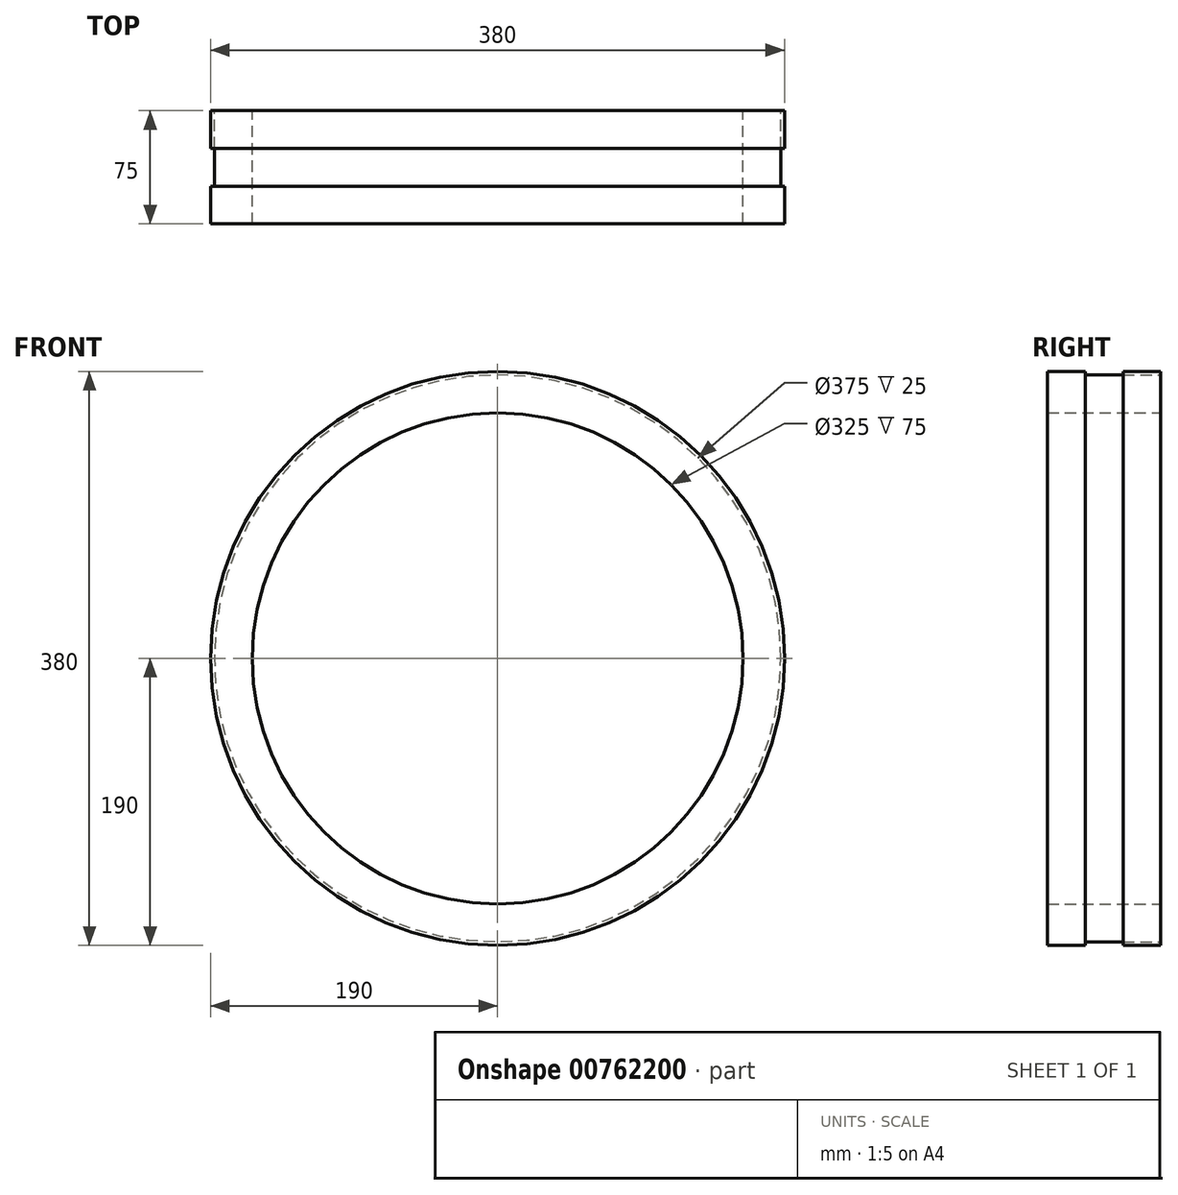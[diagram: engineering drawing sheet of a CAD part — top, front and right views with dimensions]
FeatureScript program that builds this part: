
annotation { "Feature Type Name" : "Feature", "Feature Type Description" : "" }
export const myFeature = defineFeature(function(context is Context, id is Id, definition is map)
    precondition{}
    {
        {
            var Q0;
            Q0=qCreatedBy(makeId("Front.planeOp"),FACE);
            var sketch = newSketch(context, id + "F0", { "sketchPlane" : qUnion([Q0])});
            skCircle(sketch, "E0", {"center": v(0, 0) * mm, "radius": 182.5 * mm});
            skCircle(sketch, "E1", {"center": v(0, 0) * mm, "radius": 162.5 * mm});
            skCircle(sketch, "E2", {"center": v(0, 0) * mm, "radius": 187.5 * mm});
            skLineSegment(sketch, "E3", {"start": v(0, 0) * mm, "end": v(-187.5, 0) * mm});
            skLineSegment(sketch, "E4", {"start": v(0, 0) * mm, "end": v(0, 187.5) * mm});
            skLineSegment(sketch, "E5", {"start": v(0, 0) * mm, "end": v(187.5, 0) * mm});
            skLineSegment(sketch, "E6", {"start": v(0, 0) * mm, "end": v(0, -187.5) * mm});
            skLineSegment(sketch, "E7", {"start": v(0, 0) * mm, "end": v(64.13, 176.2) * mm});
            skLineSegment(sketch, "E8", {"start": v(0, 0) * mm, "end": v(32.56, 184.65) * mm});
            skLineSegment(sketch, "E9", {"start": v(0, 0) * mm, "end": v(16.34, 186.79) * mm});
            skLineSegment(sketch, "E10", {"start": v(0, 0) * mm, "end": v(48.53, 181.11) * mm});
            skLineSegment(sketch, "E11", {"start": v(0, 0) * mm, "end": v(79.24, 169.93) * mm});
            skLineSegment(sketch, "E12", {"start": v(0, 0) * mm, "end": v(93.75, 162.38) * mm});
            skLineSegment(sketch, "E13", {"start": v(0, 0) * mm, "end": v(107.55, 153.6) * mm});
            skLineSegment(sketch, "E14", {"start": v(0, 0) * mm, "end": v(120.52, 143.63) * mm});
            skLineSegment(sketch, "E15", {"start": v(0, 0) * mm, "end": v(132.58, 132.58) * mm});
            skLineSegment(sketch, "E16", {"start": v(0, 0) * mm, "end": v(143.63, 120.52) * mm});
            skLineSegment(sketch, "E17", {"start": v(0, 0) * mm, "end": v(153.6, 107.55) * mm});
            skLineSegment(sketch, "E18", {"start": v(0, 0) * mm, "end": v(162.38, 93.75) * mm});
            skLineSegment(sketch, "E19", {"start": v(0, 0) * mm, "end": v(169.93, 79.24) * mm});
            skLineSegment(sketch, "E20", {"start": v(0, 0) * mm, "end": v(176.2, 64.13) * mm});
            skLineSegment(sketch, "E21", {"start": v(0, 0) * mm, "end": v(181.11, 48.53) * mm});
            skLineSegment(sketch, "E22", {"start": v(0, 0) * mm, "end": v(184.65, 32.56) * mm});
            skLineSegment(sketch, "E23", {"start": v(0, 0) * mm, "end": v(186.79, 16.34) * mm});
            skLineSegment(sketch, "E24", {"start": v(0, 0) * mm, "end": v(186.79, -16.34) * mm});
            skLineSegment(sketch, "E25", {"start": v(0, 0) * mm, "end": v(184.65, -32.56) * mm});
            skLineSegment(sketch, "E26", {"start": v(0, 0) * mm, "end": v(181.11, -48.53) * mm});
            skLineSegment(sketch, "E27", {"start": v(0, 0) * mm, "end": v(176.2, -64.13) * mm});
            skLineSegment(sketch, "E28", {"start": v(0, 0) * mm, "end": v(169.93, -79.24) * mm});
            skLineSegment(sketch, "E29", {"start": v(0, 0) * mm, "end": v(162.38, -93.75) * mm});
            skLineSegment(sketch, "E30", {"start": v(0, 0) * mm, "end": v(153.6, -107.55) * mm});
            skLineSegment(sketch, "E31", {"start": v(0, 0) * mm, "end": v(143.63, -120.52) * mm});
            skLineSegment(sketch, "E32", {"start": v(0, 0) * mm, "end": v(132.58, -132.58) * mm});
            skLineSegment(sketch, "E33", {"start": v(0, 0) * mm, "end": v(120.52, -143.63) * mm});
            skLineSegment(sketch, "E34", {"start": v(0, 0) * mm, "end": v(107.55, -153.6) * mm});
            skLineSegment(sketch, "E35", {"start": v(0, 0) * mm, "end": v(93.75, -162.38) * mm});
            skLineSegment(sketch, "E36", {"start": v(0, 0) * mm, "end": v(79.24, -169.93) * mm});
            skLineSegment(sketch, "E37", {"start": v(0, 0) * mm, "end": v(64.13, -176.2) * mm});
            skLineSegment(sketch, "E38", {"start": v(0, 0) * mm, "end": v(48.53, -181.11) * mm});
            skLineSegment(sketch, "E39", {"start": v(0, 0) * mm, "end": v(32.56, -184.65) * mm});
            skLineSegment(sketch, "E40", {"start": v(0, 0) * mm, "end": v(16.34, -186.79) * mm});
            skLineSegment(sketch, "E41", {"start": v(0, 0) * mm, "end": v(-16.34, -186.79) * mm});
            skLineSegment(sketch, "E42", {"start": v(0, 0) * mm, "end": v(-32.56, -184.65) * mm});
            skLineSegment(sketch, "E43", {"start": v(0, 0) * mm, "end": v(-16.34, 186.79) * mm});
            skLineSegment(sketch, "E44", {"start": v(0, 0) * mm, "end": v(-32.56, 184.65) * mm});
            skLineSegment(sketch, "E45", {"start": v(0, 0) * mm, "end": v(-48.53, 181.11) * mm});
            skLineSegment(sketch, "E46", {"start": v(-48.53, 181.11) * mm, "end": v(0, 0) * mm});
            skLineSegment(sketch, "E47", {"start": v(0, 0) * mm, "end": v(-64.13, 176.2) * mm});
            skLineSegment(sketch, "E48", {"start": v(0, 0) * mm, "end": v(-79.24, 169.93) * mm});
            skLineSegment(sketch, "E49", {"start": v(0, 0) * mm, "end": v(-93.75, 162.38) * mm});
            skLineSegment(sketch, "E50", {"start": v(0, 0) * mm, "end": v(-107.55, 153.6) * mm});
            skLineSegment(sketch, "E51", {"start": v(0, 0) * mm, "end": v(-120.52, 143.63) * mm});
            skLineSegment(sketch, "E52", {"start": v(0, 0) * mm, "end": v(-132.58, 132.58) * mm});
            skLineSegment(sketch, "E53", {"start": v(0, 0) * mm, "end": v(-143.63, 120.52) * mm});
            skLineSegment(sketch, "E54", {"start": v(0, 0) * mm, "end": v(-153.6, 107.55) * mm});
            skLineSegment(sketch, "E55", {"start": v(0, 0) * mm, "end": v(-162.38, 93.75) * mm});
            skLineSegment(sketch, "E56", {"start": v(0, 0) * mm, "end": v(-169.93, 79.24) * mm});
            skLineSegment(sketch, "E57", {"start": v(0, 0) * mm, "end": v(-176.2, 64.13) * mm});
            skLineSegment(sketch, "E58", {"start": v(0, 0) * mm, "end": v(-181.11, 48.53) * mm});
            skLineSegment(sketch, "E59", {"start": v(0, 0) * mm, "end": v(-184.65, 32.56) * mm});
            skLineSegment(sketch, "E60", {"start": v(0, 0) * mm, "end": v(-186.79, 16.34) * mm});
            skLineSegment(sketch, "E61", {"start": v(0, 0) * mm, "end": v(-48.53, -181.11) * mm});
            skLineSegment(sketch, "E62", {"start": v(0, 0) * mm, "end": v(-64.13, -176.2) * mm});
            skLineSegment(sketch, "E63", {"start": v(0, 0) * mm, "end": v(-79.24, -169.93) * mm});
            skLineSegment(sketch, "E64", {"start": v(0, 0) * mm, "end": v(-93.75, -162.38) * mm});
            skLineSegment(sketch, "E65", {"start": v(0, 0) * mm, "end": v(-107.55, -153.6) * mm});
            skLineSegment(sketch, "E66", {"start": v(0, 0) * mm, "end": v(-120.52, -143.63) * mm});
            skLineSegment(sketch, "E67", {"start": v(0, 0) * mm, "end": v(-132.58, -132.58) * mm});
            skLineSegment(sketch, "E68", {"start": v(0, 0) * mm, "end": v(-143.63, -120.52) * mm});
            skLineSegment(sketch, "E69", {"start": v(0, 0) * mm, "end": v(-153.6, -107.55) * mm});
            skLineSegment(sketch, "E70", {"start": v(0, 0) * mm, "end": v(-162.38, -93.75) * mm});
            skLineSegment(sketch, "E71", {"start": v(0, 0) * mm, "end": v(-169.93, -79.24) * mm});
            skLineSegment(sketch, "E72", {"start": v(0, 0) * mm, "end": v(-176.2, -64.13) * mm});
            skLineSegment(sketch, "E73", {"start": v(0, 0) * mm, "end": v(-181.11, -48.53) * mm});
            skLineSegment(sketch, "E74", {"start": v(0, 0) * mm, "end": v(-184.65, -32.56) * mm});
            skLineSegment(sketch, "E75", {"start": v(0, 0) * mm, "end": v(-186.79, -16.34) * mm});
            skSolve(sketch);
        }
        {
            var Q0;
            {var subQ0=sQuery(id+"F0.wireOp",EDGE,"E4");var subQ1=sQuery(id+"F0.wireOp",EDGE,"E0");var subQ2=makeQuery(id+"F0.imprint","INTERSECT",VERTEX,{"derivedFrom":[subQ1,subQ0]});Q0=makeQuery(id+"F0.imprint","IMPRINT",FACE,{"disambiguationData":[TD([[makeQuery(id+"F0.imprint","IMPRINT",EDGE,{"disambiguationData":[TD([[subQ2,-1.0]])],"derivedFrom":subQ1}),1.0]])]});}
            var Q1;
            {var subQ0=sQuery(id+"F0.wireOp",EDGE,"E9");var subQ1=sQuery(id+"F0.wireOp",EDGE,"E0");var subQ2=makeQuery(id+"F0.imprint","INTERSECT",VERTEX,{"derivedFrom":[subQ1,subQ0]});Q1=makeQuery(id+"F0.imprint","IMPRINT",FACE,{"disambiguationData":[TD([[makeQuery(id+"F0.imprint","IMPRINT",EDGE,{"disambiguationData":[TD([[subQ2,-1.0]])],"derivedFrom":subQ1}),1.0]])]});}
            var Q2;
            {var subQ0=sQuery(id+"F0.wireOp",EDGE,"E10");var subQ1=sQuery(id+"F0.wireOp",EDGE,"E0");var subQ2=makeQuery(id+"F0.imprint","INTERSECT",VERTEX,{"derivedFrom":[subQ1,subQ0]});Q2=makeQuery(id+"F0.imprint","IMPRINT",FACE,{"disambiguationData":[TD([[makeQuery(id+"F0.imprint","IMPRINT",EDGE,{"disambiguationData":[TD([[subQ2,-1.0]])],"derivedFrom":subQ1}),1.0]])]});}
            var Q3;
            {var subQ0=sQuery(id+"F0.wireOp",EDGE,"E8");var subQ1=sQuery(id+"F0.wireOp",EDGE,"E0");var subQ2=makeQuery(id+"F0.imprint","INTERSECT",VERTEX,{"derivedFrom":[subQ1,subQ0]});Q3=makeQuery(id+"F0.imprint","IMPRINT",FACE,{"disambiguationData":[TD([[makeQuery(id+"F0.imprint","IMPRINT",EDGE,{"disambiguationData":[TD([[subQ2,-1.0]])],"derivedFrom":subQ1}),1.0]])]});}
            var Q4;
            {var subQ0=sQuery(id+"F0.wireOp",EDGE,"E7");var subQ1=sQuery(id+"F0.wireOp",EDGE,"E0");var subQ2=makeQuery(id+"F0.imprint","INTERSECT",VERTEX,{"derivedFrom":[subQ1,subQ0]});Q4=makeQuery(id+"F0.imprint","IMPRINT",FACE,{"disambiguationData":[TD([[makeQuery(id+"F0.imprint","IMPRINT",EDGE,{"disambiguationData":[TD([[subQ2,-1.0]])],"derivedFrom":subQ1}),1.0]])]});}
            var Q5;
            {var subQ0=sQuery(id+"F0.wireOp",EDGE,"E11");var subQ1=sQuery(id+"F0.wireOp",EDGE,"E0");var subQ2=makeQuery(id+"F0.imprint","INTERSECT",VERTEX,{"derivedFrom":[subQ1,subQ0]});Q5=makeQuery(id+"F0.imprint","IMPRINT",FACE,{"disambiguationData":[TD([[makeQuery(id+"F0.imprint","IMPRINT",EDGE,{"disambiguationData":[TD([[subQ2,-1.0]])],"derivedFrom":subQ1}),1.0]])]});}
            var Q6;
            {var subQ0=sQuery(id+"F0.wireOp",EDGE,"E12");var subQ1=sQuery(id+"F0.wireOp",EDGE,"E0");var subQ2=makeQuery(id+"F0.imprint","INTERSECT",VERTEX,{"derivedFrom":[subQ1,subQ0]});Q6=makeQuery(id+"F0.imprint","IMPRINT",FACE,{"disambiguationData":[TD([[makeQuery(id+"F0.imprint","IMPRINT",EDGE,{"disambiguationData":[TD([[subQ2,-1.0]])],"derivedFrom":subQ1}),1.0]])]});}
            var Q7;
            {var subQ0=sQuery(id+"F0.wireOp",EDGE,"E13");var subQ1=sQuery(id+"F0.wireOp",EDGE,"E0");var subQ2=makeQuery(id+"F0.imprint","INTERSECT",VERTEX,{"derivedFrom":[subQ1,subQ0]});Q7=makeQuery(id+"F0.imprint","IMPRINT",FACE,{"disambiguationData":[TD([[makeQuery(id+"F0.imprint","IMPRINT",EDGE,{"disambiguationData":[TD([[subQ2,-1.0]])],"derivedFrom":subQ1}),1.0]])]});}
            var Q8;
            {var subQ0=sQuery(id+"F0.wireOp",EDGE,"E14");var subQ1=sQuery(id+"F0.wireOp",EDGE,"E0");var subQ2=makeQuery(id+"F0.imprint","INTERSECT",VERTEX,{"derivedFrom":[subQ1,subQ0]});Q8=makeQuery(id+"F0.imprint","IMPRINT",FACE,{"disambiguationData":[TD([[makeQuery(id+"F0.imprint","IMPRINT",EDGE,{"disambiguationData":[TD([[subQ2,-1.0]])],"derivedFrom":subQ1}),1.0]])]});}
            var Q9;
            {var subQ0=sQuery(id+"F0.wireOp",EDGE,"E15");var subQ1=sQuery(id+"F0.wireOp",EDGE,"E0");var subQ2=makeQuery(id+"F0.imprint","INTERSECT",VERTEX,{"derivedFrom":[subQ1,subQ0]});Q9=makeQuery(id+"F0.imprint","IMPRINT",FACE,{"disambiguationData":[TD([[makeQuery(id+"F0.imprint","IMPRINT",EDGE,{"disambiguationData":[TD([[subQ2,-1.0]])],"derivedFrom":subQ1}),1.0]])]});}
            var Q10;
            {var subQ0=sQuery(id+"F0.wireOp",EDGE,"E16");var subQ1=sQuery(id+"F0.wireOp",EDGE,"E0");var subQ2=makeQuery(id+"F0.imprint","INTERSECT",VERTEX,{"derivedFrom":[subQ1,subQ0]});Q10=makeQuery(id+"F0.imprint","IMPRINT",FACE,{"disambiguationData":[TD([[makeQuery(id+"F0.imprint","IMPRINT",EDGE,{"disambiguationData":[TD([[subQ2,-1.0]])],"derivedFrom":subQ1}),1.0]])]});}
            var Q11;
            {var subQ0=sQuery(id+"F0.wireOp",EDGE,"E17");var subQ1=sQuery(id+"F0.wireOp",EDGE,"E0");var subQ2=makeQuery(id+"F0.imprint","INTERSECT",VERTEX,{"derivedFrom":[subQ1,subQ0]});Q11=makeQuery(id+"F0.imprint","IMPRINT",FACE,{"disambiguationData":[TD([[makeQuery(id+"F0.imprint","IMPRINT",EDGE,{"disambiguationData":[TD([[subQ2,-1.0]])],"derivedFrom":subQ1}),1.0]])]});}
            var Q12;
            {var subQ0=sQuery(id+"F0.wireOp",EDGE,"E18");var subQ1=sQuery(id+"F0.wireOp",EDGE,"E0");var subQ2=makeQuery(id+"F0.imprint","INTERSECT",VERTEX,{"derivedFrom":[subQ1,subQ0]});Q12=makeQuery(id+"F0.imprint","IMPRINT",FACE,{"disambiguationData":[TD([[makeQuery(id+"F0.imprint","IMPRINT",EDGE,{"disambiguationData":[TD([[subQ2,-1.0]])],"derivedFrom":subQ1}),1.0]])]});}
            var Q13;
            {var subQ0=sQuery(id+"F0.wireOp",EDGE,"E20");var subQ1=sQuery(id+"F0.wireOp",EDGE,"E0");var subQ2=makeQuery(id+"F0.imprint","INTERSECT",VERTEX,{"derivedFrom":[subQ1,subQ0]});Q13=makeQuery(id+"F0.imprint","IMPRINT",FACE,{"disambiguationData":[TD([[makeQuery(id+"F0.imprint","IMPRINT",EDGE,{"disambiguationData":[TD([[subQ2,-1.0]])],"derivedFrom":subQ1}),1.0]])]});}
            var Q14;
            {var subQ0=sQuery(id+"F0.wireOp",EDGE,"E21");var subQ1=sQuery(id+"F0.wireOp",EDGE,"E0");var subQ2=makeQuery(id+"F0.imprint","INTERSECT",VERTEX,{"derivedFrom":[subQ1,subQ0]});Q14=makeQuery(id+"F0.imprint","IMPRINT",FACE,{"disambiguationData":[TD([[makeQuery(id+"F0.imprint","IMPRINT",EDGE,{"disambiguationData":[TD([[subQ2,-1.0]])],"derivedFrom":subQ1}),1.0]])]});}
            var Q15;
            {var subQ0=sQuery(id+"F0.wireOp",EDGE,"E22");var subQ1=sQuery(id+"F0.wireOp",EDGE,"E0");var subQ2=makeQuery(id+"F0.imprint","INTERSECT",VERTEX,{"derivedFrom":[subQ1,subQ0]});Q15=makeQuery(id+"F0.imprint","IMPRINT",FACE,{"disambiguationData":[TD([[makeQuery(id+"F0.imprint","IMPRINT",EDGE,{"disambiguationData":[TD([[subQ2,-1.0]])],"derivedFrom":subQ1}),1.0]])]});}
            var Q16;
            {var subQ0=sQuery(id+"F0.wireOp",EDGE,"E23");var subQ1=sQuery(id+"F0.wireOp",EDGE,"E0");var subQ2=makeQuery(id+"F0.imprint","INTERSECT",VERTEX,{"derivedFrom":[subQ1,subQ0]});Q16=makeQuery(id+"F0.imprint","IMPRINT",FACE,{"disambiguationData":[TD([[makeQuery(id+"F0.imprint","IMPRINT",EDGE,{"disambiguationData":[TD([[subQ2,-1.0]])],"derivedFrom":subQ1}),1.0]])]});}
            var Q17;
            {var subQ0=sQuery(id+"F0.wireOp",EDGE,"E23");var subQ1=sQuery(id+"F0.wireOp",EDGE,"E0");var subQ2=makeQuery(id+"F0.imprint","INTERSECT",VERTEX,{"derivedFrom":[subQ1,subQ0]});Q17=makeQuery(id+"F0.imprint","IMPRINT",FACE,{"disambiguationData":[TD([[makeQuery(id+"F0.imprint","IMPRINT",EDGE,{"disambiguationData":[TD([[subQ2,1.0]])],"derivedFrom":subQ1}),1.0]])]});}
            var Q18;
            {var subQ0=sQuery(id+"F0.wireOp",EDGE,"E5");var subQ1=sQuery(id+"F0.wireOp",EDGE,"E0");var subQ2=makeQuery(id+"F0.imprint","INTERSECT",VERTEX,{"derivedFrom":[subQ1,subQ0]});Q18=makeQuery(id+"F0.imprint","IMPRINT",FACE,{"disambiguationData":[TD([[makeQuery(id+"F0.imprint","IMPRINT",EDGE,{"disambiguationData":[TD([[subQ2,1.0]])],"derivedFrom":subQ1}),1.0]])]});}
            var Q19;
            {var subQ0=sQuery(id+"F0.wireOp",EDGE,"E3");var subQ1=sQuery(id+"F0.wireOp",EDGE,"E0");var subQ2=makeQuery(id+"F0.imprint","INTERSECT",VERTEX,{"derivedFrom":[subQ1,subQ0]});Q19=makeQuery(id+"F0.imprint","IMPRINT",FACE,{"disambiguationData":[TD([[makeQuery(id+"F0.imprint","IMPRINT",EDGE,{"disambiguationData":[TD([[subQ2,-1.0]])],"derivedFrom":subQ1}),1.0]])]});}
            var Q20;
            {var subQ0=sQuery(id+"F0.wireOp",EDGE,"E9");var subQ1=sQuery(id+"F0.wireOp",EDGE,"E0");var subQ2=makeQuery(id+"F0.imprint","INTERSECT",VERTEX,{"derivedFrom":[subQ1,subQ0]});Q20=makeQuery(id+"F0.imprint","IMPRINT",FACE,{"disambiguationData":[TD([[makeQuery(id+"F0.imprint","IMPRINT",EDGE,{"disambiguationData":[TD([[subQ2,-1.0]])],"derivedFrom":subQ1}),-1.0]])]});}
            var Q21;
            {var subQ0=sQuery(id+"F0.wireOp",EDGE,"E10");var subQ1=sQuery(id+"F0.wireOp",EDGE,"E0");var subQ2=makeQuery(id+"F0.imprint","INTERSECT",VERTEX,{"derivedFrom":[subQ1,subQ0]});Q21=makeQuery(id+"F0.imprint","IMPRINT",FACE,{"disambiguationData":[TD([[makeQuery(id+"F0.imprint","IMPRINT",EDGE,{"disambiguationData":[TD([[subQ2,-1.0]])],"derivedFrom":subQ1}),-1.0]])]});}
            var Q22;
            {var subQ0=sQuery(id+"F0.wireOp",EDGE,"E11");var subQ1=sQuery(id+"F0.wireOp",EDGE,"E0");var subQ2=makeQuery(id+"F0.imprint","INTERSECT",VERTEX,{"derivedFrom":[subQ1,subQ0]});Q22=makeQuery(id+"F0.imprint","IMPRINT",FACE,{"disambiguationData":[TD([[makeQuery(id+"F0.imprint","IMPRINT",EDGE,{"disambiguationData":[TD([[subQ2,-1.0]])],"derivedFrom":subQ1}),-1.0]])]});}
            var Q23;
            {var subQ0=sQuery(id+"F0.wireOp",EDGE,"E13");var subQ1=sQuery(id+"F0.wireOp",EDGE,"E0");var subQ2=makeQuery(id+"F0.imprint","INTERSECT",VERTEX,{"derivedFrom":[subQ1,subQ0]});Q23=makeQuery(id+"F0.imprint","IMPRINT",FACE,{"disambiguationData":[TD([[makeQuery(id+"F0.imprint","IMPRINT",EDGE,{"disambiguationData":[TD([[subQ2,-1.0]])],"derivedFrom":subQ1}),-1.0]])]});}
            var Q24;
            {var subQ0=sQuery(id+"F0.wireOp",EDGE,"E15");var subQ1=sQuery(id+"F0.wireOp",EDGE,"E0");var subQ2=makeQuery(id+"F0.imprint","INTERSECT",VERTEX,{"derivedFrom":[subQ1,subQ0]});Q24=makeQuery(id+"F0.imprint","IMPRINT",FACE,{"disambiguationData":[TD([[makeQuery(id+"F0.imprint","IMPRINT",EDGE,{"disambiguationData":[TD([[subQ2,-1.0]])],"derivedFrom":subQ1}),-1.0]])]});}
            var Q25;
            {var subQ0=sQuery(id+"F0.wireOp",EDGE,"E17");var subQ1=sQuery(id+"F0.wireOp",EDGE,"E0");var subQ2=makeQuery(id+"F0.imprint","INTERSECT",VERTEX,{"derivedFrom":[subQ1,subQ0]});Q25=makeQuery(id+"F0.imprint","IMPRINT",FACE,{"disambiguationData":[TD([[makeQuery(id+"F0.imprint","IMPRINT",EDGE,{"disambiguationData":[TD([[subQ2,-1.0]])],"derivedFrom":subQ1}),-1.0]])]});}
            var Q26;
            {var subQ0=sQuery(id+"F0.wireOp",EDGE,"E19");var subQ1=sQuery(id+"F0.wireOp",EDGE,"E0");var subQ2=makeQuery(id+"F0.imprint","INTERSECT",VERTEX,{"derivedFrom":[subQ1,subQ0]});Q26=makeQuery(id+"F0.imprint","IMPRINT",FACE,{"disambiguationData":[TD([[makeQuery(id+"F0.imprint","IMPRINT",EDGE,{"disambiguationData":[TD([[subQ2,-1.0]])],"derivedFrom":subQ1}),1.0]])]});}
            var Q27;
            {var subQ0=sQuery(id+"F0.wireOp",EDGE,"E19");var subQ1=sQuery(id+"F0.wireOp",EDGE,"E0");var subQ2=makeQuery(id+"F0.imprint","INTERSECT",VERTEX,{"derivedFrom":[subQ1,subQ0]});Q27=makeQuery(id+"F0.imprint","IMPRINT",FACE,{"disambiguationData":[TD([[makeQuery(id+"F0.imprint","IMPRINT",EDGE,{"disambiguationData":[TD([[subQ2,-1.0]])],"derivedFrom":subQ1}),-1.0]])]});}
            var Q28;
            {var subQ0=sQuery(id+"F0.wireOp",EDGE,"E21");var subQ1=sQuery(id+"F0.wireOp",EDGE,"E0");var subQ2=makeQuery(id+"F0.imprint","INTERSECT",VERTEX,{"derivedFrom":[subQ1,subQ0]});Q28=makeQuery(id+"F0.imprint","IMPRINT",FACE,{"disambiguationData":[TD([[makeQuery(id+"F0.imprint","IMPRINT",EDGE,{"disambiguationData":[TD([[subQ2,-1.0]])],"derivedFrom":subQ1}),-1.0]])]});}
            var Q29;
            {var subQ0=sQuery(id+"F0.wireOp",EDGE,"E23");var subQ1=sQuery(id+"F0.wireOp",EDGE,"E0");var subQ2=makeQuery(id+"F0.imprint","INTERSECT",VERTEX,{"derivedFrom":[subQ1,subQ0]});Q29=makeQuery(id+"F0.imprint","IMPRINT",FACE,{"disambiguationData":[TD([[makeQuery(id+"F0.imprint","IMPRINT",EDGE,{"disambiguationData":[TD([[subQ2,-1.0]])],"derivedFrom":subQ1}),-1.0]])]});}
            var Q30;
            {var subQ0=sQuery(id+"F0.wireOp",EDGE,"E6");var subQ1=sQuery(id+"F0.wireOp",EDGE,"E0");var subQ2=makeQuery(id+"F0.imprint","INTERSECT",VERTEX,{"derivedFrom":[subQ1,subQ0]});Q30=makeQuery(id+"F0.imprint","IMPRINT",FACE,{"disambiguationData":[TD([[makeQuery(id+"F0.imprint","IMPRINT",EDGE,{"disambiguationData":[TD([[subQ2,-1.0]])],"derivedFrom":subQ1}),1.0]])]});}
            var Q31;
            {var subQ0=sQuery(id+"F0.wireOp",EDGE,"E40");var subQ1=sQuery(id+"F0.wireOp",EDGE,"E0");var subQ2=makeQuery(id+"F0.imprint","INTERSECT",VERTEX,{"derivedFrom":[subQ1,subQ0]});Q31=makeQuery(id+"F0.imprint","IMPRINT",FACE,{"disambiguationData":[TD([[makeQuery(id+"F0.imprint","IMPRINT",EDGE,{"disambiguationData":[TD([[subQ2,-1.0]])],"derivedFrom":subQ1}),1.0]])]});}
            var Q32;
            {var subQ0=sQuery(id+"F0.wireOp",EDGE,"E39");var subQ1=sQuery(id+"F0.wireOp",EDGE,"E0");var subQ2=makeQuery(id+"F0.imprint","INTERSECT",VERTEX,{"derivedFrom":[subQ1,subQ0]});Q32=makeQuery(id+"F0.imprint","IMPRINT",FACE,{"disambiguationData":[TD([[makeQuery(id+"F0.imprint","IMPRINT",EDGE,{"disambiguationData":[TD([[subQ2,-1.0]])],"derivedFrom":subQ1}),1.0]])]});}
            var Q33;
            {var subQ0=sQuery(id+"F0.wireOp",EDGE,"E38");var subQ1=sQuery(id+"F0.wireOp",EDGE,"E0");var subQ2=makeQuery(id+"F0.imprint","INTERSECT",VERTEX,{"derivedFrom":[subQ1,subQ0]});Q33=makeQuery(id+"F0.imprint","IMPRINT",FACE,{"disambiguationData":[TD([[makeQuery(id+"F0.imprint","IMPRINT",EDGE,{"disambiguationData":[TD([[subQ2,-1.0]])],"derivedFrom":subQ1}),1.0]])]});}
            var Q34;
            {var subQ0=sQuery(id+"F0.wireOp",EDGE,"E37");var subQ1=sQuery(id+"F0.wireOp",EDGE,"E0");var subQ2=makeQuery(id+"F0.imprint","INTERSECT",VERTEX,{"derivedFrom":[subQ1,subQ0]});Q34=makeQuery(id+"F0.imprint","IMPRINT",FACE,{"disambiguationData":[TD([[makeQuery(id+"F0.imprint","IMPRINT",EDGE,{"disambiguationData":[TD([[subQ2,-1.0]])],"derivedFrom":subQ1}),1.0]])]});}
            var Q35;
            {var subQ0=sQuery(id+"F0.wireOp",EDGE,"E36");var subQ1=sQuery(id+"F0.wireOp",EDGE,"E0");var subQ2=makeQuery(id+"F0.imprint","INTERSECT",VERTEX,{"derivedFrom":[subQ1,subQ0]});Q35=makeQuery(id+"F0.imprint","IMPRINT",FACE,{"disambiguationData":[TD([[makeQuery(id+"F0.imprint","IMPRINT",EDGE,{"disambiguationData":[TD([[subQ2,-1.0]])],"derivedFrom":subQ1}),1.0]])]});}
            var Q36;
            {var subQ0=sQuery(id+"F0.wireOp",EDGE,"E35");var subQ1=sQuery(id+"F0.wireOp",EDGE,"E0");var subQ2=makeQuery(id+"F0.imprint","INTERSECT",VERTEX,{"derivedFrom":[subQ1,subQ0]});Q36=makeQuery(id+"F0.imprint","IMPRINT",FACE,{"disambiguationData":[TD([[makeQuery(id+"F0.imprint","IMPRINT",EDGE,{"disambiguationData":[TD([[subQ2,-1.0]])],"derivedFrom":subQ1}),1.0]])]});}
            var Q37;
            {var subQ0=sQuery(id+"F0.wireOp",EDGE,"E33");var subQ1=sQuery(id+"F0.wireOp",EDGE,"E0");var subQ2=makeQuery(id+"F0.imprint","INTERSECT",VERTEX,{"derivedFrom":[subQ1,subQ0]});Q37=makeQuery(id+"F0.imprint","IMPRINT",FACE,{"disambiguationData":[TD([[makeQuery(id+"F0.imprint","IMPRINT",EDGE,{"disambiguationData":[TD([[subQ2,-1.0]])],"derivedFrom":subQ1}),1.0]])]});}
            var Q38;
            {var subQ0=sQuery(id+"F0.wireOp",EDGE,"E32");var subQ1=sQuery(id+"F0.wireOp",EDGE,"E0");var subQ2=makeQuery(id+"F0.imprint","INTERSECT",VERTEX,{"derivedFrom":[subQ1,subQ0]});Q38=makeQuery(id+"F0.imprint","IMPRINT",FACE,{"disambiguationData":[TD([[makeQuery(id+"F0.imprint","IMPRINT",EDGE,{"disambiguationData":[TD([[subQ2,-1.0]])],"derivedFrom":subQ1}),1.0]])]});}
            var Q39;
            {var subQ0=sQuery(id+"F0.wireOp",EDGE,"E31");var subQ1=sQuery(id+"F0.wireOp",EDGE,"E0");var subQ2=makeQuery(id+"F0.imprint","INTERSECT",VERTEX,{"derivedFrom":[subQ1,subQ0]});Q39=makeQuery(id+"F0.imprint","IMPRINT",FACE,{"disambiguationData":[TD([[makeQuery(id+"F0.imprint","IMPRINT",EDGE,{"disambiguationData":[TD([[subQ2,-1.0]])],"derivedFrom":subQ1}),1.0]])]});}
            var Q40;
            {var subQ0=sQuery(id+"F0.wireOp",EDGE,"E30");var subQ1=sQuery(id+"F0.wireOp",EDGE,"E0");var subQ2=makeQuery(id+"F0.imprint","INTERSECT",VERTEX,{"derivedFrom":[subQ1,subQ0]});Q40=makeQuery(id+"F0.imprint","IMPRINT",FACE,{"disambiguationData":[TD([[makeQuery(id+"F0.imprint","IMPRINT",EDGE,{"disambiguationData":[TD([[subQ2,-1.0]])],"derivedFrom":subQ1}),1.0]])]});}
            var Q41;
            {var subQ0=sQuery(id+"F0.wireOp",EDGE,"E29");var subQ1=sQuery(id+"F0.wireOp",EDGE,"E0");var subQ2=makeQuery(id+"F0.imprint","INTERSECT",VERTEX,{"derivedFrom":[subQ1,subQ0]});Q41=makeQuery(id+"F0.imprint","IMPRINT",FACE,{"disambiguationData":[TD([[makeQuery(id+"F0.imprint","IMPRINT",EDGE,{"disambiguationData":[TD([[subQ2,-1.0]])],"derivedFrom":subQ1}),1.0]])]});}
            var Q42;
            {var subQ0=sQuery(id+"F0.wireOp",EDGE,"E28");var subQ1=sQuery(id+"F0.wireOp",EDGE,"E0");var subQ2=makeQuery(id+"F0.imprint","INTERSECT",VERTEX,{"derivedFrom":[subQ1,subQ0]});Q42=makeQuery(id+"F0.imprint","IMPRINT",FACE,{"disambiguationData":[TD([[makeQuery(id+"F0.imprint","IMPRINT",EDGE,{"disambiguationData":[TD([[subQ2,-1.0]])],"derivedFrom":subQ1}),1.0]])]});}
            var Q43;
            {var subQ0=sQuery(id+"F0.wireOp",EDGE,"E25");var subQ1=sQuery(id+"F0.wireOp",EDGE,"E0");var subQ2=makeQuery(id+"F0.imprint","INTERSECT",VERTEX,{"derivedFrom":[subQ1,subQ0]});Q43=makeQuery(id+"F0.imprint","IMPRINT",FACE,{"disambiguationData":[TD([[makeQuery(id+"F0.imprint","IMPRINT",EDGE,{"disambiguationData":[TD([[subQ2,-1.0]])],"derivedFrom":subQ1}),1.0]])]});}
            var Q44;
            {var subQ0=sQuery(id+"F0.wireOp",EDGE,"E26");var subQ1=sQuery(id+"F0.wireOp",EDGE,"E0");var subQ2=makeQuery(id+"F0.imprint","INTERSECT",VERTEX,{"derivedFrom":[subQ1,subQ0]});Q44=makeQuery(id+"F0.imprint","IMPRINT",FACE,{"disambiguationData":[TD([[makeQuery(id+"F0.imprint","IMPRINT",EDGE,{"disambiguationData":[TD([[subQ2,-1.0]])],"derivedFrom":subQ1}),1.0]])]});}
            var Q45;
            {var subQ0=sQuery(id+"F0.wireOp",EDGE,"E27");var subQ1=sQuery(id+"F0.wireOp",EDGE,"E0");var subQ2=makeQuery(id+"F0.imprint","INTERSECT",VERTEX,{"derivedFrom":[subQ1,subQ0]});Q45=makeQuery(id+"F0.imprint","IMPRINT",FACE,{"disambiguationData":[TD([[makeQuery(id+"F0.imprint","IMPRINT",EDGE,{"disambiguationData":[TD([[subQ2,-1.0]])],"derivedFrom":subQ1}),1.0]])]});}
            var Q46;
            {var subQ0=sQuery(id+"F0.wireOp",EDGE,"E34");var subQ1=sQuery(id+"F0.wireOp",EDGE,"E0");var subQ2=makeQuery(id+"F0.imprint","INTERSECT",VERTEX,{"derivedFrom":[subQ1,subQ0]});Q46=makeQuery(id+"F0.imprint","IMPRINT",FACE,{"disambiguationData":[TD([[makeQuery(id+"F0.imprint","IMPRINT",EDGE,{"disambiguationData":[TD([[subQ2,-1.0]])],"derivedFrom":subQ1}),1.0]])]});}
            var Q47;
            {var subQ0=sQuery(id+"F0.wireOp",EDGE,"E5");var subQ1=sQuery(id+"F0.wireOp",EDGE,"E0");var subQ2=makeQuery(id+"F0.imprint","INTERSECT",VERTEX,{"derivedFrom":[subQ1,subQ0]});Q47=makeQuery(id+"F0.imprint","IMPRINT",FACE,{"disambiguationData":[TD([[makeQuery(id+"F0.imprint","IMPRINT",EDGE,{"disambiguationData":[TD([[subQ2,1.0]])],"derivedFrom":subQ1}),-1.0]])]});}
            var Q48;
            {var subQ0=sQuery(id+"F0.wireOp",EDGE,"E26");var subQ1=sQuery(id+"F0.wireOp",EDGE,"E0");var subQ2=makeQuery(id+"F0.imprint","INTERSECT",VERTEX,{"derivedFrom":[subQ1,subQ0]});Q48=makeQuery(id+"F0.imprint","IMPRINT",FACE,{"disambiguationData":[TD([[makeQuery(id+"F0.imprint","IMPRINT",EDGE,{"disambiguationData":[TD([[subQ2,-1.0]])],"derivedFrom":subQ1}),-1.0]])]});}
            var Q49;
            {var subQ0=sQuery(id+"F0.wireOp",EDGE,"E28");var subQ1=sQuery(id+"F0.wireOp",EDGE,"E0");var subQ2=makeQuery(id+"F0.imprint","INTERSECT",VERTEX,{"derivedFrom":[subQ1,subQ0]});Q49=makeQuery(id+"F0.imprint","IMPRINT",FACE,{"disambiguationData":[TD([[makeQuery(id+"F0.imprint","IMPRINT",EDGE,{"disambiguationData":[TD([[subQ2,-1.0]])],"derivedFrom":subQ1}),-1.0]])]});}
            var Q50;
            {var subQ0=sQuery(id+"F0.wireOp",EDGE,"E30");var subQ1=sQuery(id+"F0.wireOp",EDGE,"E0");var subQ2=makeQuery(id+"F0.imprint","INTERSECT",VERTEX,{"derivedFrom":[subQ1,subQ0]});Q50=makeQuery(id+"F0.imprint","IMPRINT",FACE,{"disambiguationData":[TD([[makeQuery(id+"F0.imprint","IMPRINT",EDGE,{"disambiguationData":[TD([[subQ2,-1.0]])],"derivedFrom":subQ1}),-1.0]])]});}
            var Q51;
            {var subQ0=sQuery(id+"F0.wireOp",EDGE,"E32");var subQ1=sQuery(id+"F0.wireOp",EDGE,"E0");var subQ2=makeQuery(id+"F0.imprint","INTERSECT",VERTEX,{"derivedFrom":[subQ1,subQ0]});Q51=makeQuery(id+"F0.imprint","IMPRINT",FACE,{"disambiguationData":[TD([[makeQuery(id+"F0.imprint","IMPRINT",EDGE,{"disambiguationData":[TD([[subQ2,-1.0]])],"derivedFrom":subQ1}),-1.0]])]});}
            var Q52;
            {var subQ0=sQuery(id+"F0.wireOp",EDGE,"E34");var subQ1=sQuery(id+"F0.wireOp",EDGE,"E0");var subQ2=makeQuery(id+"F0.imprint","INTERSECT",VERTEX,{"derivedFrom":[subQ1,subQ0]});Q52=makeQuery(id+"F0.imprint","IMPRINT",FACE,{"disambiguationData":[TD([[makeQuery(id+"F0.imprint","IMPRINT",EDGE,{"disambiguationData":[TD([[subQ2,-1.0]])],"derivedFrom":subQ1}),-1.0]])]});}
            var Q53;
            {var subQ0=sQuery(id+"F0.wireOp",EDGE,"E36");var subQ1=sQuery(id+"F0.wireOp",EDGE,"E0");var subQ2=makeQuery(id+"F0.imprint","INTERSECT",VERTEX,{"derivedFrom":[subQ1,subQ0]});Q53=makeQuery(id+"F0.imprint","IMPRINT",FACE,{"disambiguationData":[TD([[makeQuery(id+"F0.imprint","IMPRINT",EDGE,{"disambiguationData":[TD([[subQ2,-1.0]])],"derivedFrom":subQ1}),-1.0]])]});}
            var Q54;
            {var subQ0=sQuery(id+"F0.wireOp",EDGE,"E38");var subQ1=sQuery(id+"F0.wireOp",EDGE,"E0");var subQ2=makeQuery(id+"F0.imprint","INTERSECT",VERTEX,{"derivedFrom":[subQ1,subQ0]});Q54=makeQuery(id+"F0.imprint","IMPRINT",FACE,{"disambiguationData":[TD([[makeQuery(id+"F0.imprint","IMPRINT",EDGE,{"disambiguationData":[TD([[subQ2,-1.0]])],"derivedFrom":subQ1}),-1.0]])]});}
            var Q55;
            {var subQ0=sQuery(id+"F0.wireOp",EDGE,"E40");var subQ1=sQuery(id+"F0.wireOp",EDGE,"E0");var subQ2=makeQuery(id+"F0.imprint","INTERSECT",VERTEX,{"derivedFrom":[subQ1,subQ0]});Q55=makeQuery(id+"F0.imprint","IMPRINT",FACE,{"disambiguationData":[TD([[makeQuery(id+"F0.imprint","IMPRINT",EDGE,{"disambiguationData":[TD([[subQ2,-1.0]])],"derivedFrom":subQ1}),-1.0]])]});}
            var Q56;
            {var subQ0=sQuery(id+"F0.wireOp",EDGE,"E43");var subQ1=sQuery(id+"F0.wireOp",EDGE,"E0");var subQ2=makeQuery(id+"F0.imprint","INTERSECT",VERTEX,{"derivedFrom":[subQ1,subQ0]});Q56=makeQuery(id+"F0.imprint","IMPRINT",FACE,{"disambiguationData":[TD([[makeQuery(id+"F0.imprint","IMPRINT",EDGE,{"disambiguationData":[TD([[subQ2,-1.0]])],"derivedFrom":subQ1}),1.0]])]});}
            var Q57;
            {var subQ0=sQuery(id+"F0.wireOp",EDGE,"E44");var subQ1=sQuery(id+"F0.wireOp",EDGE,"E0");var subQ2=makeQuery(id+"F0.imprint","INTERSECT",VERTEX,{"derivedFrom":[subQ1,subQ0]});Q57=makeQuery(id+"F0.imprint","IMPRINT",FACE,{"disambiguationData":[TD([[makeQuery(id+"F0.imprint","IMPRINT",EDGE,{"disambiguationData":[TD([[subQ2,-1.0]])],"derivedFrom":subQ1}),1.0]])]});}
            var Q58;
            {var subQ0=sQuery(id+"F0.wireOp",EDGE,"E46");var subQ1=sQuery(id+"F0.wireOp",EDGE,"E0");var subQ2=makeQuery(id+"F0.imprint","INTERSECT",VERTEX,{"derivedFrom":[subQ1,subQ0]});Q58=makeQuery(id+"F0.imprint","IMPRINT",FACE,{"disambiguationData":[TD([[makeQuery(id+"F0.imprint","IMPRINT",EDGE,{"disambiguationData":[TD([[subQ2,-1.0]])],"derivedFrom":subQ1}),1.0]])]});}
            var Q59;
            {var subQ0=sQuery(id+"F0.wireOp",EDGE,"E47");var subQ1=sQuery(id+"F0.wireOp",EDGE,"E0");var subQ2=makeQuery(id+"F0.imprint","INTERSECT",VERTEX,{"derivedFrom":[subQ1,subQ0]});Q59=makeQuery(id+"F0.imprint","IMPRINT",FACE,{"disambiguationData":[TD([[makeQuery(id+"F0.imprint","IMPRINT",EDGE,{"disambiguationData":[TD([[subQ2,-1.0]])],"derivedFrom":subQ1}),1.0]])]});}
            var Q60;
            {var subQ0=sQuery(id+"F0.wireOp",EDGE,"E48");var subQ1=sQuery(id+"F0.wireOp",EDGE,"E0");var subQ2=makeQuery(id+"F0.imprint","INTERSECT",VERTEX,{"derivedFrom":[subQ1,subQ0]});Q60=makeQuery(id+"F0.imprint","IMPRINT",FACE,{"disambiguationData":[TD([[makeQuery(id+"F0.imprint","IMPRINT",EDGE,{"disambiguationData":[TD([[subQ2,-1.0]])],"derivedFrom":subQ1}),1.0]])]});}
            var Q61;
            {var subQ0=sQuery(id+"F0.wireOp",EDGE,"E49");var subQ1=sQuery(id+"F0.wireOp",EDGE,"E0");var subQ2=makeQuery(id+"F0.imprint","INTERSECT",VERTEX,{"derivedFrom":[subQ1,subQ0]});Q61=makeQuery(id+"F0.imprint","IMPRINT",FACE,{"disambiguationData":[TD([[makeQuery(id+"F0.imprint","IMPRINT",EDGE,{"disambiguationData":[TD([[subQ2,-1.0]])],"derivedFrom":subQ1}),1.0]])]});}
            var Q62;
            {var subQ0=sQuery(id+"F0.wireOp",EDGE,"E50");var subQ1=sQuery(id+"F0.wireOp",EDGE,"E0");var subQ2=makeQuery(id+"F0.imprint","INTERSECT",VERTEX,{"derivedFrom":[subQ1,subQ0]});Q62=makeQuery(id+"F0.imprint","IMPRINT",FACE,{"disambiguationData":[TD([[makeQuery(id+"F0.imprint","IMPRINT",EDGE,{"disambiguationData":[TD([[subQ2,-1.0]])],"derivedFrom":subQ1}),1.0]])]});}
            var Q63;
            {var subQ0=sQuery(id+"F0.wireOp",EDGE,"E52");var subQ1=sQuery(id+"F0.wireOp",EDGE,"E0");var subQ2=makeQuery(id+"F0.imprint","INTERSECT",VERTEX,{"derivedFrom":[subQ1,subQ0]});Q63=makeQuery(id+"F0.imprint","IMPRINT",FACE,{"disambiguationData":[TD([[makeQuery(id+"F0.imprint","IMPRINT",EDGE,{"disambiguationData":[TD([[subQ2,-1.0]])],"derivedFrom":subQ1}),1.0]])]});}
            var Q64;
            {var subQ0=sQuery(id+"F0.wireOp",EDGE,"E53");var subQ1=sQuery(id+"F0.wireOp",EDGE,"E0");var subQ2=makeQuery(id+"F0.imprint","INTERSECT",VERTEX,{"derivedFrom":[subQ1,subQ0]});Q64=makeQuery(id+"F0.imprint","IMPRINT",FACE,{"disambiguationData":[TD([[makeQuery(id+"F0.imprint","IMPRINT",EDGE,{"disambiguationData":[TD([[subQ2,-1.0]])],"derivedFrom":subQ1}),1.0]])]});}
            var Q65;
            {var subQ0=sQuery(id+"F0.wireOp",EDGE,"E54");var subQ1=sQuery(id+"F0.wireOp",EDGE,"E0");var subQ2=makeQuery(id+"F0.imprint","INTERSECT",VERTEX,{"derivedFrom":[subQ1,subQ0]});Q65=makeQuery(id+"F0.imprint","IMPRINT",FACE,{"disambiguationData":[TD([[makeQuery(id+"F0.imprint","IMPRINT",EDGE,{"disambiguationData":[TD([[subQ2,-1.0]])],"derivedFrom":subQ1}),1.0]])]});}
            var Q66;
            {var subQ0=sQuery(id+"F0.wireOp",EDGE,"E55");var subQ1=sQuery(id+"F0.wireOp",EDGE,"E0");var subQ2=makeQuery(id+"F0.imprint","INTERSECT",VERTEX,{"derivedFrom":[subQ1,subQ0]});Q66=makeQuery(id+"F0.imprint","IMPRINT",FACE,{"disambiguationData":[TD([[makeQuery(id+"F0.imprint","IMPRINT",EDGE,{"disambiguationData":[TD([[subQ2,-1.0]])],"derivedFrom":subQ1}),1.0]])]});}
            var Q67;
            {var subQ0=sQuery(id+"F0.wireOp",EDGE,"E56");var subQ1=sQuery(id+"F0.wireOp",EDGE,"E0");var subQ2=makeQuery(id+"F0.imprint","INTERSECT",VERTEX,{"derivedFrom":[subQ1,subQ0]});Q67=makeQuery(id+"F0.imprint","IMPRINT",FACE,{"disambiguationData":[TD([[makeQuery(id+"F0.imprint","IMPRINT",EDGE,{"disambiguationData":[TD([[subQ2,-1.0]])],"derivedFrom":subQ1}),1.0]])]});}
            var Q68;
            {var subQ0=sQuery(id+"F0.wireOp",EDGE,"E57");var subQ1=sQuery(id+"F0.wireOp",EDGE,"E0");var subQ2=makeQuery(id+"F0.imprint","INTERSECT",VERTEX,{"derivedFrom":[subQ1,subQ0]});Q68=makeQuery(id+"F0.imprint","IMPRINT",FACE,{"disambiguationData":[TD([[makeQuery(id+"F0.imprint","IMPRINT",EDGE,{"disambiguationData":[TD([[subQ2,-1.0]])],"derivedFrom":subQ1}),1.0]])]});}
            var Q69;
            {var subQ0=sQuery(id+"F0.wireOp",EDGE,"E58");var subQ1=sQuery(id+"F0.wireOp",EDGE,"E0");var subQ2=makeQuery(id+"F0.imprint","INTERSECT",VERTEX,{"derivedFrom":[subQ1,subQ0]});Q69=makeQuery(id+"F0.imprint","IMPRINT",FACE,{"disambiguationData":[TD([[makeQuery(id+"F0.imprint","IMPRINT",EDGE,{"disambiguationData":[TD([[subQ2,-1.0]])],"derivedFrom":subQ1}),1.0]])]});}
            var Q70;
            {var subQ0=sQuery(id+"F0.wireOp",EDGE,"E59");var subQ1=sQuery(id+"F0.wireOp",EDGE,"E0");var subQ2=makeQuery(id+"F0.imprint","INTERSECT",VERTEX,{"derivedFrom":[subQ1,subQ0]});Q70=makeQuery(id+"F0.imprint","IMPRINT",FACE,{"disambiguationData":[TD([[makeQuery(id+"F0.imprint","IMPRINT",EDGE,{"disambiguationData":[TD([[subQ2,-1.0]])],"derivedFrom":subQ1}),1.0]])]});}
            var Q71;
            {var subQ0=sQuery(id+"F0.wireOp",EDGE,"E60");var subQ1=sQuery(id+"F0.wireOp",EDGE,"E0");var subQ2=makeQuery(id+"F0.imprint","INTERSECT",VERTEX,{"derivedFrom":[subQ1,subQ0]});Q71=makeQuery(id+"F0.imprint","IMPRINT",FACE,{"disambiguationData":[TD([[makeQuery(id+"F0.imprint","IMPRINT",EDGE,{"disambiguationData":[TD([[subQ2,-1.0]])],"derivedFrom":subQ1}),1.0]])]});}
            var Q72;
            {var subQ0=sQuery(id+"F0.wireOp",EDGE,"E51");var subQ1=sQuery(id+"F0.wireOp",EDGE,"E0");var subQ2=makeQuery(id+"F0.imprint","INTERSECT",VERTEX,{"derivedFrom":[subQ1,subQ0]});Q72=makeQuery(id+"F0.imprint","IMPRINT",FACE,{"disambiguationData":[TD([[makeQuery(id+"F0.imprint","IMPRINT",EDGE,{"disambiguationData":[TD([[subQ2,-1.0]])],"derivedFrom":subQ1}),1.0]])]});}
            var Q73;
            {var subQ0=sQuery(id+"F0.wireOp",EDGE,"E75");var subQ1=sQuery(id+"F0.wireOp",EDGE,"E0");var subQ2=makeQuery(id+"F0.imprint","INTERSECT",VERTEX,{"derivedFrom":[subQ1,subQ0]});Q73=makeQuery(id+"F0.imprint","IMPRINT",FACE,{"disambiguationData":[TD([[makeQuery(id+"F0.imprint","IMPRINT",EDGE,{"disambiguationData":[TD([[subQ2,-1.0]])],"derivedFrom":subQ1}),1.0]])]});}
            var Q74;
            {var subQ0=sQuery(id+"F0.wireOp",EDGE,"E74");var subQ1=sQuery(id+"F0.wireOp",EDGE,"E0");var subQ2=makeQuery(id+"F0.imprint","INTERSECT",VERTEX,{"derivedFrom":[subQ1,subQ0]});Q74=makeQuery(id+"F0.imprint","IMPRINT",FACE,{"disambiguationData":[TD([[makeQuery(id+"F0.imprint","IMPRINT",EDGE,{"disambiguationData":[TD([[subQ2,-1.0]])],"derivedFrom":subQ1}),1.0]])]});}
            var Q75;
            {var subQ0=sQuery(id+"F0.wireOp",EDGE,"E73");var subQ1=sQuery(id+"F0.wireOp",EDGE,"E0");var subQ2=makeQuery(id+"F0.imprint","INTERSECT",VERTEX,{"derivedFrom":[subQ1,subQ0]});Q75=makeQuery(id+"F0.imprint","IMPRINT",FACE,{"disambiguationData":[TD([[makeQuery(id+"F0.imprint","IMPRINT",EDGE,{"disambiguationData":[TD([[subQ2,-1.0]])],"derivedFrom":subQ1}),1.0]])]});}
            var Q76;
            {var subQ0=sQuery(id+"F0.wireOp",EDGE,"E72");var subQ1=sQuery(id+"F0.wireOp",EDGE,"E0");var subQ2=makeQuery(id+"F0.imprint","INTERSECT",VERTEX,{"derivedFrom":[subQ1,subQ0]});Q76=makeQuery(id+"F0.imprint","IMPRINT",FACE,{"disambiguationData":[TD([[makeQuery(id+"F0.imprint","IMPRINT",EDGE,{"disambiguationData":[TD([[subQ2,-1.0]])],"derivedFrom":subQ1}),1.0]])]});}
            var Q77;
            {var subQ0=sQuery(id+"F0.wireOp",EDGE,"E71");var subQ1=sQuery(id+"F0.wireOp",EDGE,"E0");var subQ2=makeQuery(id+"F0.imprint","INTERSECT",VERTEX,{"derivedFrom":[subQ1,subQ0]});Q77=makeQuery(id+"F0.imprint","IMPRINT",FACE,{"disambiguationData":[TD([[makeQuery(id+"F0.imprint","IMPRINT",EDGE,{"disambiguationData":[TD([[subQ2,-1.0]])],"derivedFrom":subQ1}),1.0]])]});}
            var Q78;
            {var subQ0=sQuery(id+"F0.wireOp",EDGE,"E70");var subQ1=sQuery(id+"F0.wireOp",EDGE,"E0");var subQ2=makeQuery(id+"F0.imprint","INTERSECT",VERTEX,{"derivedFrom":[subQ1,subQ0]});Q78=makeQuery(id+"F0.imprint","IMPRINT",FACE,{"disambiguationData":[TD([[makeQuery(id+"F0.imprint","IMPRINT",EDGE,{"disambiguationData":[TD([[subQ2,-1.0]])],"derivedFrom":subQ1}),1.0]])]});}
            var Q79;
            {var subQ0=sQuery(id+"F0.wireOp",EDGE,"E69");var subQ1=sQuery(id+"F0.wireOp",EDGE,"E0");var subQ2=makeQuery(id+"F0.imprint","INTERSECT",VERTEX,{"derivedFrom":[subQ1,subQ0]});Q79=makeQuery(id+"F0.imprint","IMPRINT",FACE,{"disambiguationData":[TD([[makeQuery(id+"F0.imprint","IMPRINT",EDGE,{"disambiguationData":[TD([[subQ2,-1.0]])],"derivedFrom":subQ1}),1.0]])]});}
            var Q80;
            {var subQ0=sQuery(id+"F0.wireOp",EDGE,"E68");var subQ1=sQuery(id+"F0.wireOp",EDGE,"E0");var subQ2=makeQuery(id+"F0.imprint","INTERSECT",VERTEX,{"derivedFrom":[subQ1,subQ0]});Q80=makeQuery(id+"F0.imprint","IMPRINT",FACE,{"disambiguationData":[TD([[makeQuery(id+"F0.imprint","IMPRINT",EDGE,{"disambiguationData":[TD([[subQ2,-1.0]])],"derivedFrom":subQ1}),1.0]])]});}
            var Q81;
            {var subQ0=sQuery(id+"F0.wireOp",EDGE,"E67");var subQ1=sQuery(id+"F0.wireOp",EDGE,"E0");var subQ2=makeQuery(id+"F0.imprint","INTERSECT",VERTEX,{"derivedFrom":[subQ1,subQ0]});Q81=makeQuery(id+"F0.imprint","IMPRINT",FACE,{"disambiguationData":[TD([[makeQuery(id+"F0.imprint","IMPRINT",EDGE,{"disambiguationData":[TD([[subQ2,-1.0]])],"derivedFrom":subQ1}),1.0]])]});}
            var Q82;
            {var subQ0=sQuery(id+"F0.wireOp",EDGE,"E66");var subQ1=sQuery(id+"F0.wireOp",EDGE,"E0");var subQ2=makeQuery(id+"F0.imprint","INTERSECT",VERTEX,{"derivedFrom":[subQ1,subQ0]});Q82=makeQuery(id+"F0.imprint","IMPRINT",FACE,{"disambiguationData":[TD([[makeQuery(id+"F0.imprint","IMPRINT",EDGE,{"disambiguationData":[TD([[subQ2,-1.0]])],"derivedFrom":subQ1}),1.0]])]});}
            var Q83;
            {var subQ0=sQuery(id+"F0.wireOp",EDGE,"E65");var subQ1=sQuery(id+"F0.wireOp",EDGE,"E0");var subQ2=makeQuery(id+"F0.imprint","INTERSECT",VERTEX,{"derivedFrom":[subQ1,subQ0]});Q83=makeQuery(id+"F0.imprint","IMPRINT",FACE,{"disambiguationData":[TD([[makeQuery(id+"F0.imprint","IMPRINT",EDGE,{"disambiguationData":[TD([[subQ2,-1.0]])],"derivedFrom":subQ1}),1.0]])]});}
            var Q84;
            {var subQ0=sQuery(id+"F0.wireOp",EDGE,"E64");var subQ1=sQuery(id+"F0.wireOp",EDGE,"E0");var subQ2=makeQuery(id+"F0.imprint","INTERSECT",VERTEX,{"derivedFrom":[subQ1,subQ0]});Q84=makeQuery(id+"F0.imprint","IMPRINT",FACE,{"disambiguationData":[TD([[makeQuery(id+"F0.imprint","IMPRINT",EDGE,{"disambiguationData":[TD([[subQ2,-1.0]])],"derivedFrom":subQ1}),1.0]])]});}
            var Q85;
            {var subQ0=sQuery(id+"F0.wireOp",EDGE,"E63");var subQ1=sQuery(id+"F0.wireOp",EDGE,"E0");var subQ2=makeQuery(id+"F0.imprint","INTERSECT",VERTEX,{"derivedFrom":[subQ1,subQ0]});Q85=makeQuery(id+"F0.imprint","IMPRINT",FACE,{"disambiguationData":[TD([[makeQuery(id+"F0.imprint","IMPRINT",EDGE,{"disambiguationData":[TD([[subQ2,-1.0]])],"derivedFrom":subQ1}),1.0]])]});}
            var Q86;
            {var subQ0=sQuery(id+"F0.wireOp",EDGE,"E62");var subQ1=sQuery(id+"F0.wireOp",EDGE,"E0");var subQ2=makeQuery(id+"F0.imprint","INTERSECT",VERTEX,{"derivedFrom":[subQ1,subQ0]});Q86=makeQuery(id+"F0.imprint","IMPRINT",FACE,{"disambiguationData":[TD([[makeQuery(id+"F0.imprint","IMPRINT",EDGE,{"disambiguationData":[TD([[subQ2,-1.0]])],"derivedFrom":subQ1}),1.0]])]});}
            var Q87;
            {var subQ0=sQuery(id+"F0.wireOp",EDGE,"E61");var subQ1=sQuery(id+"F0.wireOp",EDGE,"E0");var subQ2=makeQuery(id+"F0.imprint","INTERSECT",VERTEX,{"derivedFrom":[subQ1,subQ0]});Q87=makeQuery(id+"F0.imprint","IMPRINT",FACE,{"disambiguationData":[TD([[makeQuery(id+"F0.imprint","IMPRINT",EDGE,{"disambiguationData":[TD([[subQ2,-1.0]])],"derivedFrom":subQ1}),1.0]])]});}
            var Q88;
            {var subQ0=sQuery(id+"F0.wireOp",EDGE,"E42");var subQ1=sQuery(id+"F0.wireOp",EDGE,"E0");var subQ2=makeQuery(id+"F0.imprint","INTERSECT",VERTEX,{"derivedFrom":[subQ1,subQ0]});Q88=makeQuery(id+"F0.imprint","IMPRINT",FACE,{"disambiguationData":[TD([[makeQuery(id+"F0.imprint","IMPRINT",EDGE,{"disambiguationData":[TD([[subQ2,-1.0]])],"derivedFrom":subQ1}),1.0]])]});}
            var Q89;
            {var subQ0=sQuery(id+"F0.wireOp",EDGE,"E41");var subQ1=sQuery(id+"F0.wireOp",EDGE,"E0");var subQ2=makeQuery(id+"F0.imprint","INTERSECT",VERTEX,{"derivedFrom":[subQ1,subQ0]});Q89=makeQuery(id+"F0.imprint","IMPRINT",FACE,{"disambiguationData":[TD([[makeQuery(id+"F0.imprint","IMPRINT",EDGE,{"disambiguationData":[TD([[subQ2,-1.0]])],"derivedFrom":subQ1}),1.0]])]});}
            var Q90;
            {var subQ0=sQuery(id+"F0.wireOp",EDGE,"E43");var subQ1=sQuery(id+"F0.wireOp",EDGE,"E0");var subQ2=makeQuery(id+"F0.imprint","INTERSECT",VERTEX,{"derivedFrom":[subQ1,subQ0]});Q90=makeQuery(id+"F0.imprint","IMPRINT",FACE,{"disambiguationData":[TD([[makeQuery(id+"F0.imprint","IMPRINT",EDGE,{"disambiguationData":[TD([[subQ2,-1.0]])],"derivedFrom":subQ1}),-1.0]])]});}
            var Q91;
            {var subQ0=sQuery(id+"F0.wireOp",EDGE,"E46");var subQ1=sQuery(id+"F0.wireOp",EDGE,"E0");var subQ2=makeQuery(id+"F0.imprint","INTERSECT",VERTEX,{"derivedFrom":[subQ1,subQ0]});Q91=makeQuery(id+"F0.imprint","IMPRINT",FACE,{"disambiguationData":[TD([[makeQuery(id+"F0.imprint","IMPRINT",EDGE,{"disambiguationData":[TD([[subQ2,-1.0]])],"derivedFrom":subQ1}),-1.0]])]});}
            var Q92;
            {var subQ0=sQuery(id+"F0.wireOp",EDGE,"E48");var subQ1=sQuery(id+"F0.wireOp",EDGE,"E0");var subQ2=makeQuery(id+"F0.imprint","INTERSECT",VERTEX,{"derivedFrom":[subQ1,subQ0]});Q92=makeQuery(id+"F0.imprint","IMPRINT",FACE,{"disambiguationData":[TD([[makeQuery(id+"F0.imprint","IMPRINT",EDGE,{"disambiguationData":[TD([[subQ2,-1.0]])],"derivedFrom":subQ1}),-1.0]])]});}
            var Q93;
            {var subQ0=sQuery(id+"F0.wireOp",EDGE,"E50");var subQ1=sQuery(id+"F0.wireOp",EDGE,"E0");var subQ2=makeQuery(id+"F0.imprint","INTERSECT",VERTEX,{"derivedFrom":[subQ1,subQ0]});Q93=makeQuery(id+"F0.imprint","IMPRINT",FACE,{"disambiguationData":[TD([[makeQuery(id+"F0.imprint","IMPRINT",EDGE,{"disambiguationData":[TD([[subQ2,-1.0]])],"derivedFrom":subQ1}),-1.0]])]});}
            var Q94;
            {var subQ0=sQuery(id+"F0.wireOp",EDGE,"E52");var subQ1=sQuery(id+"F0.wireOp",EDGE,"E0");var subQ2=makeQuery(id+"F0.imprint","INTERSECT",VERTEX,{"derivedFrom":[subQ1,subQ0]});Q94=makeQuery(id+"F0.imprint","IMPRINT",FACE,{"disambiguationData":[TD([[makeQuery(id+"F0.imprint","IMPRINT",EDGE,{"disambiguationData":[TD([[subQ2,-1.0]])],"derivedFrom":subQ1}),-1.0]])]});}
            var Q95;
            {var subQ0=sQuery(id+"F0.wireOp",EDGE,"E54");var subQ1=sQuery(id+"F0.wireOp",EDGE,"E0");var subQ2=makeQuery(id+"F0.imprint","INTERSECT",VERTEX,{"derivedFrom":[subQ1,subQ0]});Q95=makeQuery(id+"F0.imprint","IMPRINT",FACE,{"disambiguationData":[TD([[makeQuery(id+"F0.imprint","IMPRINT",EDGE,{"disambiguationData":[TD([[subQ2,-1.0]])],"derivedFrom":subQ1}),-1.0]])]});}
            var Q96;
            {var subQ0=sQuery(id+"F0.wireOp",EDGE,"E56");var subQ1=sQuery(id+"F0.wireOp",EDGE,"E0");var subQ2=makeQuery(id+"F0.imprint","INTERSECT",VERTEX,{"derivedFrom":[subQ1,subQ0]});Q96=makeQuery(id+"F0.imprint","IMPRINT",FACE,{"disambiguationData":[TD([[makeQuery(id+"F0.imprint","IMPRINT",EDGE,{"disambiguationData":[TD([[subQ2,-1.0]])],"derivedFrom":subQ1}),-1.0]])]});}
            var Q97;
            {var subQ0=sQuery(id+"F0.wireOp",EDGE,"E58");var subQ1=sQuery(id+"F0.wireOp",EDGE,"E0");var subQ2=makeQuery(id+"F0.imprint","INTERSECT",VERTEX,{"derivedFrom":[subQ1,subQ0]});Q97=makeQuery(id+"F0.imprint","IMPRINT",FACE,{"disambiguationData":[TD([[makeQuery(id+"F0.imprint","IMPRINT",EDGE,{"disambiguationData":[TD([[subQ2,-1.0]])],"derivedFrom":subQ1}),-1.0]])]});}
            var Q98;
            {var subQ0=sQuery(id+"F0.wireOp",EDGE,"E60");var subQ1=sQuery(id+"F0.wireOp",EDGE,"E0");var subQ2=makeQuery(id+"F0.imprint","INTERSECT",VERTEX,{"derivedFrom":[subQ1,subQ0]});Q98=makeQuery(id+"F0.imprint","IMPRINT",FACE,{"disambiguationData":[TD([[makeQuery(id+"F0.imprint","IMPRINT",EDGE,{"disambiguationData":[TD([[subQ2,-1.0]])],"derivedFrom":subQ1}),-1.0]])]});}
            var Q99;
            {var subQ0=sQuery(id+"F0.wireOp",EDGE,"E75");var subQ1=sQuery(id+"F0.wireOp",EDGE,"E0");var subQ2=makeQuery(id+"F0.imprint","INTERSECT",VERTEX,{"derivedFrom":[subQ1,subQ0]});Q99=makeQuery(id+"F0.imprint","IMPRINT",FACE,{"disambiguationData":[TD([[makeQuery(id+"F0.imprint","IMPRINT",EDGE,{"disambiguationData":[TD([[subQ2,-1.0]])],"derivedFrom":subQ1}),-1.0]])]});}
            var Q100;
            {var subQ0=sQuery(id+"F0.wireOp",EDGE,"E73");var subQ1=sQuery(id+"F0.wireOp",EDGE,"E0");var subQ2=makeQuery(id+"F0.imprint","INTERSECT",VERTEX,{"derivedFrom":[subQ1,subQ0]});Q100=makeQuery(id+"F0.imprint","IMPRINT",FACE,{"disambiguationData":[TD([[makeQuery(id+"F0.imprint","IMPRINT",EDGE,{"disambiguationData":[TD([[subQ2,-1.0]])],"derivedFrom":subQ1}),-1.0]])]});}
            var Q101;
            {var subQ0=sQuery(id+"F0.wireOp",EDGE,"E71");var subQ1=sQuery(id+"F0.wireOp",EDGE,"E0");var subQ2=makeQuery(id+"F0.imprint","INTERSECT",VERTEX,{"derivedFrom":[subQ1,subQ0]});Q101=makeQuery(id+"F0.imprint","IMPRINT",FACE,{"disambiguationData":[TD([[makeQuery(id+"F0.imprint","IMPRINT",EDGE,{"disambiguationData":[TD([[subQ2,-1.0]])],"derivedFrom":subQ1}),-1.0]])]});}
            var Q102;
            {var subQ0=sQuery(id+"F0.wireOp",EDGE,"E69");var subQ1=sQuery(id+"F0.wireOp",EDGE,"E0");var subQ2=makeQuery(id+"F0.imprint","INTERSECT",VERTEX,{"derivedFrom":[subQ1,subQ0]});Q102=makeQuery(id+"F0.imprint","IMPRINT",FACE,{"disambiguationData":[TD([[makeQuery(id+"F0.imprint","IMPRINT",EDGE,{"disambiguationData":[TD([[subQ2,-1.0]])],"derivedFrom":subQ1}),-1.0]])]});}
            var Q103;
            {var subQ0=sQuery(id+"F0.wireOp",EDGE,"E67");var subQ1=sQuery(id+"F0.wireOp",EDGE,"E0");var subQ2=makeQuery(id+"F0.imprint","INTERSECT",VERTEX,{"derivedFrom":[subQ1,subQ0]});Q103=makeQuery(id+"F0.imprint","IMPRINT",FACE,{"disambiguationData":[TD([[makeQuery(id+"F0.imprint","IMPRINT",EDGE,{"disambiguationData":[TD([[subQ2,-1.0]])],"derivedFrom":subQ1}),-1.0]])]});}
            var Q104;
            {var subQ0=sQuery(id+"F0.wireOp",EDGE,"E65");var subQ1=sQuery(id+"F0.wireOp",EDGE,"E0");var subQ2=makeQuery(id+"F0.imprint","INTERSECT",VERTEX,{"derivedFrom":[subQ1,subQ0]});Q104=makeQuery(id+"F0.imprint","IMPRINT",FACE,{"disambiguationData":[TD([[makeQuery(id+"F0.imprint","IMPRINT",EDGE,{"disambiguationData":[TD([[subQ2,-1.0]])],"derivedFrom":subQ1}),-1.0]])]});}
            var Q105;
            {var subQ0=sQuery(id+"F0.wireOp",EDGE,"E63");var subQ1=sQuery(id+"F0.wireOp",EDGE,"E0");var subQ2=makeQuery(id+"F0.imprint","INTERSECT",VERTEX,{"derivedFrom":[subQ1,subQ0]});Q105=makeQuery(id+"F0.imprint","IMPRINT",FACE,{"disambiguationData":[TD([[makeQuery(id+"F0.imprint","IMPRINT",EDGE,{"disambiguationData":[TD([[subQ2,-1.0]])],"derivedFrom":subQ1}),-1.0]])]});}
            var Q106;
            {var subQ0=sQuery(id+"F0.wireOp",EDGE,"E61");var subQ1=sQuery(id+"F0.wireOp",EDGE,"E0");var subQ2=makeQuery(id+"F0.imprint","INTERSECT",VERTEX,{"derivedFrom":[subQ1,subQ0]});Q106=makeQuery(id+"F0.imprint","IMPRINT",FACE,{"disambiguationData":[TD([[makeQuery(id+"F0.imprint","IMPRINT",EDGE,{"disambiguationData":[TD([[subQ2,-1.0]])],"derivedFrom":subQ1}),-1.0]])]});}
            var Q107;
            {var subQ0=sQuery(id+"F0.wireOp",EDGE,"E41");var subQ1=sQuery(id+"F0.wireOp",EDGE,"E0");var subQ2=makeQuery(id+"F0.imprint","INTERSECT",VERTEX,{"derivedFrom":[subQ1,subQ0]});Q107=makeQuery(id+"F0.imprint","IMPRINT",FACE,{"disambiguationData":[TD([[makeQuery(id+"F0.imprint","IMPRINT",EDGE,{"disambiguationData":[TD([[subQ2,-1.0]])],"derivedFrom":subQ1}),-1.0]])]});}
            extrude(context, id + "F1", {"entities" : qUnion([Q0, Q1, Q2, Q3, Q4, Q5, Q6, Q7, Q8, Q9, Q10, Q11, Q12, Q13, Q14, Q15, Q16, Q17, Q18, Q19, Q20, Q21, Q22, Q23, Q24, Q25, Q26, Q27, Q28, Q29, Q30, Q31, Q32, Q33, Q34, Q35, Q36, Q37, Q38, Q39, Q40, Q41, Q42, Q43, Q44, Q45, Q46, Q47, Q48, Q49, Q50, Q51, Q52, Q53, Q54, Q55, Q56, Q57, Q58, Q59, Q60, Q61, Q62, Q63, Q64, Q65, Q66, Q67, Q68, Q69, Q70, Q71, Q72, Q73, Q74, Q75, Q76, Q77, Q78, Q79, Q80, Q81, Q82, Q83, Q84, Q85, Q86, Q87, Q88, Q89, Q90, Q91, Q92, Q93, Q94, Q95, Q96, Q97, Q98, Q99, Q100, Q101, Q102, Q103, Q104, Q105, Q106, Q107]), "depth" : 25 * mm, "offsetDistance" : 25 * mm});
        }
        {
            var Q0;
            Q0=makeQuery(id+"F1.opExtrude","CAP_FACE",FACE,{"disambiguationData":[OSD([sQuery(id+"F0.wireOp",EDGE,"E0"),sQuery(id+"F0.wireOp",EDGE,"E1"),sQuery(id+"F0.wireOp",EDGE,"E2"),sQuery(id+"F0.wireOp",EDGE,"E3"),sQuery(id+"F0.wireOp",EDGE,"E4"),sQuery(id+"F0.wireOp",EDGE,"E5"),sQuery(id+"F0.wireOp",EDGE,"E6"),sQuery(id+"F0.wireOp",EDGE,"E7"),sQuery(id+"F0.wireOp",EDGE,"E8"),sQuery(id+"F0.wireOp",EDGE,"E9"),sQuery(id+"F0.wireOp",EDGE,"E10"),sQuery(id+"F0.wireOp",EDGE,"E11"),sQuery(id+"F0.wireOp",EDGE,"E12"),sQuery(id+"F0.wireOp",EDGE,"E13"),sQuery(id+"F0.wireOp",EDGE,"E14"),sQuery(id+"F0.wireOp",EDGE,"E15"),sQuery(id+"F0.wireOp",EDGE,"E16"),sQuery(id+"F0.wireOp",EDGE,"E17"),sQuery(id+"F0.wireOp",EDGE,"E18"),sQuery(id+"F0.wireOp",EDGE,"E19"),sQuery(id+"F0.wireOp",EDGE,"E20"),sQuery(id+"F0.wireOp",EDGE,"E21"),sQuery(id+"F0.wireOp",EDGE,"E22"),sQuery(id+"F0.wireOp",EDGE,"E23"),sQuery(id+"F0.wireOp",EDGE,"E24"),sQuery(id+"F0.wireOp",EDGE,"E25"),sQuery(id+"F0.wireOp",EDGE,"E26"),sQuery(id+"F0.wireOp",EDGE,"E27"),sQuery(id+"F0.wireOp",EDGE,"E28"),sQuery(id+"F0.wireOp",EDGE,"E29"),sQuery(id+"F0.wireOp",EDGE,"E30"),sQuery(id+"F0.wireOp",EDGE,"E31"),sQuery(id+"F0.wireOp",EDGE,"E32"),sQuery(id+"F0.wireOp",EDGE,"E33"),sQuery(id+"F0.wireOp",EDGE,"E34"),sQuery(id+"F0.wireOp",EDGE,"E35"),sQuery(id+"F0.wireOp",EDGE,"E36"),sQuery(id+"F0.wireOp",EDGE,"E37"),sQuery(id+"F0.wireOp",EDGE,"E38"),sQuery(id+"F0.wireOp",EDGE,"E39"),sQuery(id+"F0.wireOp",EDGE,"E40"),sQuery(id+"F0.wireOp",EDGE,"E41"),sQuery(id+"F0.wireOp",EDGE,"E42"),sQuery(id+"F0.wireOp",EDGE,"E43"),sQuery(id+"F0.wireOp",EDGE,"E44"),sQuery(id+"F0.wireOp",EDGE,"E46"),sQuery(id+"F0.wireOp",EDGE,"E47"),sQuery(id+"F0.wireOp",EDGE,"E48"),sQuery(id+"F0.wireOp",EDGE,"E49"),sQuery(id+"F0.wireOp",EDGE,"E50"),sQuery(id+"F0.wireOp",EDGE,"E51"),sQuery(id+"F0.wireOp",EDGE,"E52"),sQuery(id+"F0.wireOp",EDGE,"E53"),sQuery(id+"F0.wireOp",EDGE,"E54"),sQuery(id+"F0.wireOp",EDGE,"E55"),sQuery(id+"F0.wireOp",EDGE,"E56"),sQuery(id+"F0.wireOp",EDGE,"E57"),sQuery(id+"F0.wireOp",EDGE,"E58"),sQuery(id+"F0.wireOp",EDGE,"E59"),sQuery(id+"F0.wireOp",EDGE,"E60"),sQuery(id+"F0.wireOp",EDGE,"E61"),sQuery(id+"F0.wireOp",EDGE,"E62"),sQuery(id+"F0.wireOp",EDGE,"E63"),sQuery(id+"F0.wireOp",EDGE,"E64"),sQuery(id+"F0.wireOp",EDGE,"E65"),sQuery(id+"F0.wireOp",EDGE,"E66"),sQuery(id+"F0.wireOp",EDGE,"E67"),sQuery(id+"F0.wireOp",EDGE,"E68"),sQuery(id+"F0.wireOp",EDGE,"E69"),sQuery(id+"F0.wireOp",EDGE,"E70"),sQuery(id+"F0.wireOp",EDGE,"E71"),sQuery(id+"F0.wireOp",EDGE,"E72"),sQuery(id+"F0.wireOp",EDGE,"E73"),sQuery(id+"F0.wireOp",EDGE,"E74"),sQuery(id+"F0.wireOp",EDGE,"E75")])],"isStart":false});
            var sketch = newSketch(context, id + "F2", { "sketchPlane" : qUnion([Q0])});
            skCircle(sketch, "E76", {"center": v(0, 0) * mm, "radius": 162.5 * mm});
            skCircle(sketch, "E77", {"center": v(0, 0) * mm, "radius": 190 * mm});
            skSolve(sketch);
        }
        {
            var Q0;
            Q0=makeQuery(id+"F2.imprint","IMPRINT",FACE,{"disambiguationData":[TD([[makeQuery(id+"F2.imprint","IMPRINT",EDGE,{"derivedFrom":sQuery(id+"F2.wireOp",EDGE,"E77")}),1.0]])]});
            var Q1;
            Q1=makeQuery(id+"F2.imprint","IMPRINT",FACE,{"disambiguationData":[TD([[makeQuery(id+"F2.imprint","IMPRINT",EDGE,{"derivedFrom":sQuery(id+"F2.wireOp",EDGE,"E76")}),-1.0]])]});
            extrude(context, id + "F3", {"entities" : qUnion([Q0, Q1]), "operationType" : NewBodyOperationType.ADD, "depth" : 25 * mm, "offsetDistance" : 25 * mm});
        }
        {
            var Q0;
            Q0=makeQuery(id+"F1.opExtrude","CAP_FACE",FACE,{"disambiguationData":[OSD([sQuery(id+"F0.wireOp",EDGE,"E0"),sQuery(id+"F0.wireOp",EDGE,"E1"),sQuery(id+"F0.wireOp",EDGE,"E2"),sQuery(id+"F0.wireOp",EDGE,"E3"),sQuery(id+"F0.wireOp",EDGE,"E4"),sQuery(id+"F0.wireOp",EDGE,"E5"),sQuery(id+"F0.wireOp",EDGE,"E6"),sQuery(id+"F0.wireOp",EDGE,"E7"),sQuery(id+"F0.wireOp",EDGE,"E8"),sQuery(id+"F0.wireOp",EDGE,"E9"),sQuery(id+"F0.wireOp",EDGE,"E10"),sQuery(id+"F0.wireOp",EDGE,"E11"),sQuery(id+"F0.wireOp",EDGE,"E12"),sQuery(id+"F0.wireOp",EDGE,"E13"),sQuery(id+"F0.wireOp",EDGE,"E14"),sQuery(id+"F0.wireOp",EDGE,"E15"),sQuery(id+"F0.wireOp",EDGE,"E16"),sQuery(id+"F0.wireOp",EDGE,"E17"),sQuery(id+"F0.wireOp",EDGE,"E18"),sQuery(id+"F0.wireOp",EDGE,"E19"),sQuery(id+"F0.wireOp",EDGE,"E20"),sQuery(id+"F0.wireOp",EDGE,"E21"),sQuery(id+"F0.wireOp",EDGE,"E22"),sQuery(id+"F0.wireOp",EDGE,"E23"),sQuery(id+"F0.wireOp",EDGE,"E24"),sQuery(id+"F0.wireOp",EDGE,"E25"),sQuery(id+"F0.wireOp",EDGE,"E26"),sQuery(id+"F0.wireOp",EDGE,"E27"),sQuery(id+"F0.wireOp",EDGE,"E28"),sQuery(id+"F0.wireOp",EDGE,"E29"),sQuery(id+"F0.wireOp",EDGE,"E30"),sQuery(id+"F0.wireOp",EDGE,"E31"),sQuery(id+"F0.wireOp",EDGE,"E32"),sQuery(id+"F0.wireOp",EDGE,"E33"),sQuery(id+"F0.wireOp",EDGE,"E34"),sQuery(id+"F0.wireOp",EDGE,"E35"),sQuery(id+"F0.wireOp",EDGE,"E36"),sQuery(id+"F0.wireOp",EDGE,"E37"),sQuery(id+"F0.wireOp",EDGE,"E38"),sQuery(id+"F0.wireOp",EDGE,"E39"),sQuery(id+"F0.wireOp",EDGE,"E40"),sQuery(id+"F0.wireOp",EDGE,"E41"),sQuery(id+"F0.wireOp",EDGE,"E42"),sQuery(id+"F0.wireOp",EDGE,"E43"),sQuery(id+"F0.wireOp",EDGE,"E44"),sQuery(id+"F0.wireOp",EDGE,"E46"),sQuery(id+"F0.wireOp",EDGE,"E47"),sQuery(id+"F0.wireOp",EDGE,"E48"),sQuery(id+"F0.wireOp",EDGE,"E49"),sQuery(id+"F0.wireOp",EDGE,"E50"),sQuery(id+"F0.wireOp",EDGE,"E51"),sQuery(id+"F0.wireOp",EDGE,"E52"),sQuery(id+"F0.wireOp",EDGE,"E53"),sQuery(id+"F0.wireOp",EDGE,"E54"),sQuery(id+"F0.wireOp",EDGE,"E55"),sQuery(id+"F0.wireOp",EDGE,"E56"),sQuery(id+"F0.wireOp",EDGE,"E57"),sQuery(id+"F0.wireOp",EDGE,"E58"),sQuery(id+"F0.wireOp",EDGE,"E59"),sQuery(id+"F0.wireOp",EDGE,"E60"),sQuery(id+"F0.wireOp",EDGE,"E61"),sQuery(id+"F0.wireOp",EDGE,"E62"),sQuery(id+"F0.wireOp",EDGE,"E63"),sQuery(id+"F0.wireOp",EDGE,"E64"),sQuery(id+"F0.wireOp",EDGE,"E65"),sQuery(id+"F0.wireOp",EDGE,"E66"),sQuery(id+"F0.wireOp",EDGE,"E67"),sQuery(id+"F0.wireOp",EDGE,"E68"),sQuery(id+"F0.wireOp",EDGE,"E69"),sQuery(id+"F0.wireOp",EDGE,"E70"),sQuery(id+"F0.wireOp",EDGE,"E71"),sQuery(id+"F0.wireOp",EDGE,"E72"),sQuery(id+"F0.wireOp",EDGE,"E73"),sQuery(id+"F0.wireOp",EDGE,"E74"),sQuery(id+"F0.wireOp",EDGE,"E75")])],"isStart":true});
            extrude(context, id + "F4", {"entities" : qUnion([Q0]), "operationType" : NewBodyOperationType.ADD, "depth" : 25 * mm, "offsetDistance" : 25 * mm});
        }
        {
            var Q0;
            Q0=makeQuery(id+"F4.opExtrude","CAP_FACE",FACE,{"disambiguationData":[OSD([sQuery(id+"F0.wireOp",EDGE,"E0"),sQuery(id+"F0.wireOp",EDGE,"E1"),sQuery(id+"F0.wireOp",EDGE,"E2"),sQuery(id+"F0.wireOp",EDGE,"E3"),sQuery(id+"F0.wireOp",EDGE,"E4"),sQuery(id+"F0.wireOp",EDGE,"E5"),sQuery(id+"F0.wireOp",EDGE,"E6"),sQuery(id+"F0.wireOp",EDGE,"E7"),sQuery(id+"F0.wireOp",EDGE,"E8"),sQuery(id+"F0.wireOp",EDGE,"E9"),sQuery(id+"F0.wireOp",EDGE,"E10"),sQuery(id+"F0.wireOp",EDGE,"E11"),sQuery(id+"F0.wireOp",EDGE,"E12"),sQuery(id+"F0.wireOp",EDGE,"E13"),sQuery(id+"F0.wireOp",EDGE,"E14"),sQuery(id+"F0.wireOp",EDGE,"E15"),sQuery(id+"F0.wireOp",EDGE,"E16"),sQuery(id+"F0.wireOp",EDGE,"E17"),sQuery(id+"F0.wireOp",EDGE,"E18"),sQuery(id+"F0.wireOp",EDGE,"E19"),sQuery(id+"F0.wireOp",EDGE,"E20"),sQuery(id+"F0.wireOp",EDGE,"E21"),sQuery(id+"F0.wireOp",EDGE,"E22"),sQuery(id+"F0.wireOp",EDGE,"E23"),sQuery(id+"F0.wireOp",EDGE,"E24"),sQuery(id+"F0.wireOp",EDGE,"E25"),sQuery(id+"F0.wireOp",EDGE,"E26"),sQuery(id+"F0.wireOp",EDGE,"E27"),sQuery(id+"F0.wireOp",EDGE,"E28"),sQuery(id+"F0.wireOp",EDGE,"E29"),sQuery(id+"F0.wireOp",EDGE,"E30"),sQuery(id+"F0.wireOp",EDGE,"E31"),sQuery(id+"F0.wireOp",EDGE,"E32"),sQuery(id+"F0.wireOp",EDGE,"E33"),sQuery(id+"F0.wireOp",EDGE,"E34"),sQuery(id+"F0.wireOp",EDGE,"E35"),sQuery(id+"F0.wireOp",EDGE,"E36"),sQuery(id+"F0.wireOp",EDGE,"E37"),sQuery(id+"F0.wireOp",EDGE,"E38"),sQuery(id+"F0.wireOp",EDGE,"E39"),sQuery(id+"F0.wireOp",EDGE,"E40"),sQuery(id+"F0.wireOp",EDGE,"E41"),sQuery(id+"F0.wireOp",EDGE,"E42"),sQuery(id+"F0.wireOp",EDGE,"E43"),sQuery(id+"F0.wireOp",EDGE,"E44"),sQuery(id+"F0.wireOp",EDGE,"E46"),sQuery(id+"F0.wireOp",EDGE,"E47"),sQuery(id+"F0.wireOp",EDGE,"E48"),sQuery(id+"F0.wireOp",EDGE,"E49"),sQuery(id+"F0.wireOp",EDGE,"E50"),sQuery(id+"F0.wireOp",EDGE,"E51"),sQuery(id+"F0.wireOp",EDGE,"E52"),sQuery(id+"F0.wireOp",EDGE,"E53"),sQuery(id+"F0.wireOp",EDGE,"E54"),sQuery(id+"F0.wireOp",EDGE,"E55"),sQuery(id+"F0.wireOp",EDGE,"E56"),sQuery(id+"F0.wireOp",EDGE,"E57"),sQuery(id+"F0.wireOp",EDGE,"E58"),sQuery(id+"F0.wireOp",EDGE,"E59"),sQuery(id+"F0.wireOp",EDGE,"E60"),sQuery(id+"F0.wireOp",EDGE,"E61"),sQuery(id+"F0.wireOp",EDGE,"E62"),sQuery(id+"F0.wireOp",EDGE,"E63"),sQuery(id+"F0.wireOp",EDGE,"E64"),sQuery(id+"F0.wireOp",EDGE,"E65"),sQuery(id+"F0.wireOp",EDGE,"E66"),sQuery(id+"F0.wireOp",EDGE,"E67"),sQuery(id+"F0.wireOp",EDGE,"E68"),sQuery(id+"F0.wireOp",EDGE,"E69"),sQuery(id+"F0.wireOp",EDGE,"E70"),sQuery(id+"F0.wireOp",EDGE,"E71"),sQuery(id+"F0.wireOp",EDGE,"E72"),sQuery(id+"F0.wireOp",EDGE,"E73"),sQuery(id+"F0.wireOp",EDGE,"E74"),sQuery(id+"F0.wireOp",EDGE,"E75")])],"isStart":false});
            var sketch = newSketch(context, id + "F5", { "sketchPlane" : qUnion([Q0])});
            skCircle(sketch, "E78", {"center": v(0, 0) * mm, "radius": 190 * mm});
            skSolve(sketch);
        }
        {
            var Q0;
            Q0=makeQuery(id+"F5.imprint","IMPRINT",FACE,{"disambiguationData":[TD([[makeQuery(id+"F5.imprint","IMPRINT",EDGE,{"derivedFrom":sQuery(id+"F5.wireOp",EDGE,"E78")}),1.0]])]});
            extrude(context, id + "F6", {"entities" : qUnion([Q0]), "oppositeDirection" : true, "depth" : 25 * mm, "offsetDistance" : 25 * mm});
        }
    });
